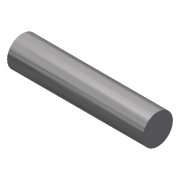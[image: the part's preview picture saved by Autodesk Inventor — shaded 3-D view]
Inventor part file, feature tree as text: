
AUTODESK INVENTOR PART (.ipt)
format: ipt  version: 2016 (Build 200138000, 138)  size: 74,240 bytes
history: native  units: in
note: dims shown in document units (in); Inventor stores cm internally (conversion verified against a paired STEP export)
features: extrude x1, sketch x1
ambient origin geometry x8: Origin, YZ Plane, XZ Plane, XY Plane, X Axis, Y Axis, Z Axis, Center Point
bodies: Solid1 (feature_tree)
feature tree (2):
  extrude  "Extrusion1"  Depth=1.6875in TaperAngle=0.0deg
  sketch  "Sketch1"  dims[d0=0.375in d1=1.6875in d2=0.0in]
